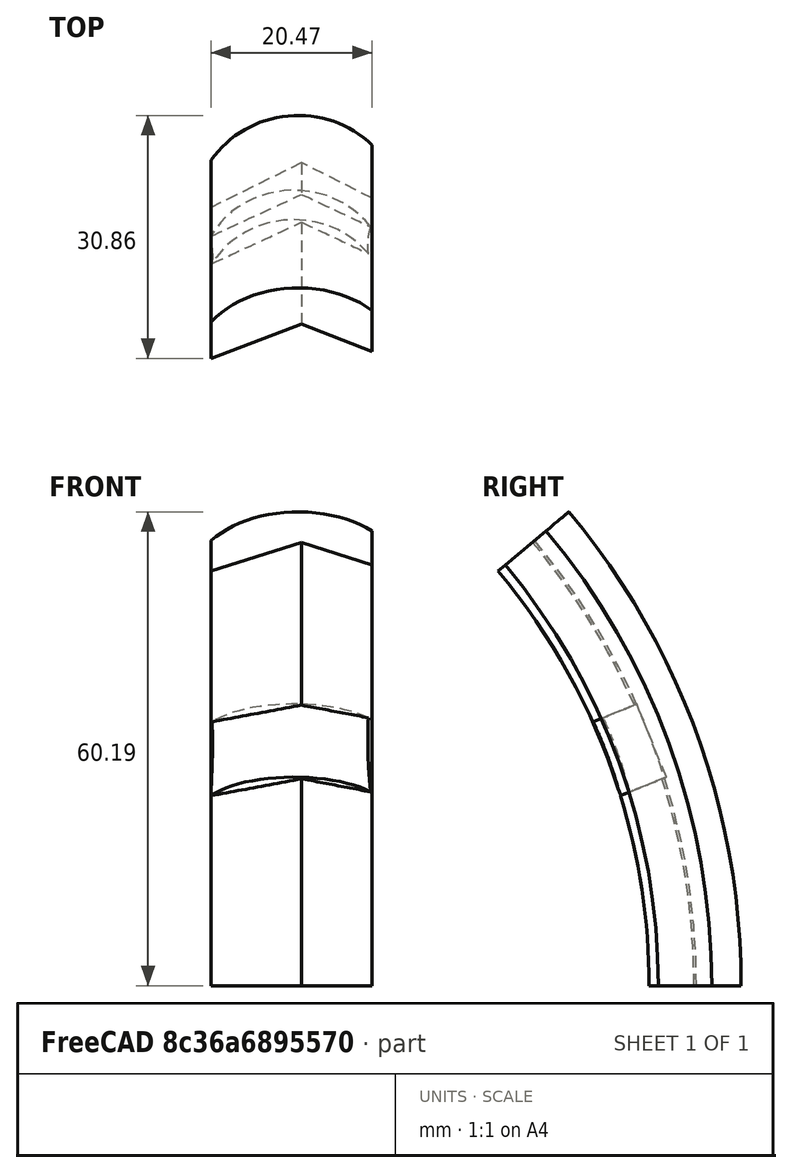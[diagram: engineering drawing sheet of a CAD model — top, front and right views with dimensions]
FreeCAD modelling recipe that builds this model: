
FCSTD DOCUMENT  (FreeCAD 0.16R)
Label: headphonepatch
License: All rights reserved
LicenseURL: http://en.wikipedia.org/wiki/All_rights_reserved
objects: Sketcher::SketchObject×1, PartDesign::Revolution×1, Part::Cylinder×1, Part::Cut×1, Mesh::Feature×1
note: 5 computed .brp shape members not serialized (recipe doc carries the construction recipe); baked Part::Feature solids carry a one-line shape summary decoded from their .brp

FEATURE [Sketcher::SketchObject] Sketch
  sketch-geometry (5):
    g0: LineSegment StartX=8.9553 StartY=83.1085 StartZ=0 EndX=0.00401435 EndY=87.631 EndZ=0
    g1: LineSegment StartX=0.00401435 StartY=87.631 StartZ=0 EndX=-11.5073 EndY=81.9394 EndZ=0
    g2: ArcOfCircle CenterX=-0.431287 CenterY=80 CenterZ=0 NormalX=0 NormalY=0 NormalZ=1 Radius=13.6349 StartAngle=0.811486 EndAngle=2.51893
    g3: LineSegment StartX=-11.5073 StartY=81.9394 StartZ=0 EndX=-11.5073 EndY=87.952 EndZ=0
    g4: LineSegment StartX=8.9553 StartY=89.8896 StartZ=0 EndX=8.9553 EndY=83.1085 EndZ=0
  constraints (16):
    c: Coincident(g1,g0)
    c: DistanceX(g2) = 8.9553
    c: DistanceX(g2) = -11.5073
    c: Coincident(g3,g1)
    c: Coincident(g3,g2)
    c: Vertical(g3)
    c: Coincident(g4,g2)
    c: Coincident(g4,g0)
    c: Vertical(g4)
    c: Distance(g1) = 12.8415
    c: Distance(g0) = 10.0289
    c: Distance(g2,g0) = 7.00734
    c: Distance(g3) = 6.01251
    c: Distance(g4) = 6.78111
    c: Distance(g2,g1) = 6.64761
    c: DistanceY(g2) = 80
FEATURE [PartDesign::Revolution] Revolution
  Angle = 40
  Axis = (1,0,0)
  Base = (0,0,0)
  ReferenceAxis = -> Sketch [H_Axis]
  Sketch = -> Sketch
FEATURE [Part::Cylinder] Cylinder
  Angle = 360
  Height = 10
  Placement = pos=(-1,73,22) rot=(1,0,0;0.383972rad)
  Radius = 12
FEATURE [Part::Cut] Cut
  Base = -> Revolution
  Tool = -> Cylinder
FEATURE [Mesh::Feature] Mesh  label="Cut (Meshed)"
